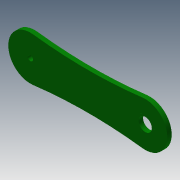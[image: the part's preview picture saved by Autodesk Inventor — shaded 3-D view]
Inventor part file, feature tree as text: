
AUTODESK INVENTOR PART (.ipt)
format: ipt  version: 2013 (Build 170138000, 138)  size: 275,456 bytes
history: native  units: mm
features: sketch x18, extrude x17
ambient origin geometry x8: Origin, YZ Plane, XZ Plane, XY Plane, X Axis, Y Axis, Z Axis, Center Point
bodies: Solid1 (feature_tree)
feature tree (35):
  extrude  "Extrusion1"  Depth=50.0mm
  extrude  "Extrusion2"  Depth=6.0mm
  extrude  "Extrusion3"  Depth=5.0mm TaperAngle=0.0deg
  extrude  "Extrusion4"  Depth=20.0mm
  extrude  "Extrusion5"  Depth=20.0mm
  extrude  "Extrusion6"  Depth=3.0mm
  sketch  "Sketch7"  dims[d22=3.0mm d23=5.0mm d24=0.0mm]
  extrude  "Extrusion7"  Depth=5.0mm TaperAngle=0.0deg
  extrude  "Extrusion8"  Depth=1.0mm
  extrude  "Extrusion9"  Depth=1.0mm
  extrude  "Extrusion10"  Depth=15.0mm
  extrude  "Extrusion11"  Depth=5.0mm TaperAngle=0.0deg
  sketch  "Sketch12"  dims[d44=1.0mm d45=1.0mm]
  sketch  "Sketch13"  dims[d46=1.0mm d47=5.0mm d48=0.0mm]
  extrude  "Extrusion12"  Depth=1.0mm
  extrude  "Extrusion13"  Depth=5.0mm TaperAngle=0.0deg
  extrude  "Extrusion14"  Depth=5.0mm TaperAngle=0.0deg
  extrude  "Extrusion15"  Depth=5.0mm TaperAngle=0.0deg
  extrude  "Extrusion16"  Depth=43.308mm
  extrude  "Extrusion18"  Depth=20.0mm
  sketch  "Sketch1"  dims[d0=150.0mm d1=50.0mm]
  sketch  "Sketch2"  dims[d2=5.0mm d3=0.0mm d4=6.0mm]
  sketch  "Sketch3"  dims[d5=6.0mm d6=5.0mm d7=0.0mm]
  sketch  "Sketch4"  dims[d11=55.0mm d12=20.0mm]
  sketch  "Sketch5"  dims[d13=40.2mm d14=20.0mm]
  sketch  "Sketch6"  dims[d20=3.0mm d21=3.0mm]
  sketch  "Sketch8"  dims[d32=5.0mm d33=0.0mm d34=1.0mm]
  sketch  "Sketch9"  dims[d35=1.0mm d36=1.0mm]
  sketch  "Sketch10"  dims[d37=5.0mm d38=0.0mm d39=15.0mm]
  sketch  "Sketch11"  dims[d40=15.0mm d41=5.0mm d42=0.0mm]
  sketch  "Sketch14"  dims[d49=5.0mm d50=0.0mm d51=5.0mm d52=0.0mm]
  sketch  "Sketch15"  dims[d53=130.0mm d54=5.0mm d55=0.0mm]
  sketch  "Sketch16"  dims[d56=15.0mm d57=43.308mm]
  sketch  "Sketch17"  dims[d58=40.2mm d59=20.0mm]
  sketch  "Sketch19"  dims[d60=5.0mm d61=0.0mm d62=33.15mm d63=18.1mm d64=55.0mm d65=40.2mm d66=20.0mm d67=5.0mm d68=0.0mm d69=33.15mm d70=18.1mm d71=55.0mm d72=40.2mm d73=20.0mm d74=5.0mm d75=0.0mm d76=5.0mm d77=0.0mm d84=5.0mm d85=0.0mm d86=5.0mm d87=0.0mm d98=6.0mm d99=5.0mm d100=0.0mm]
